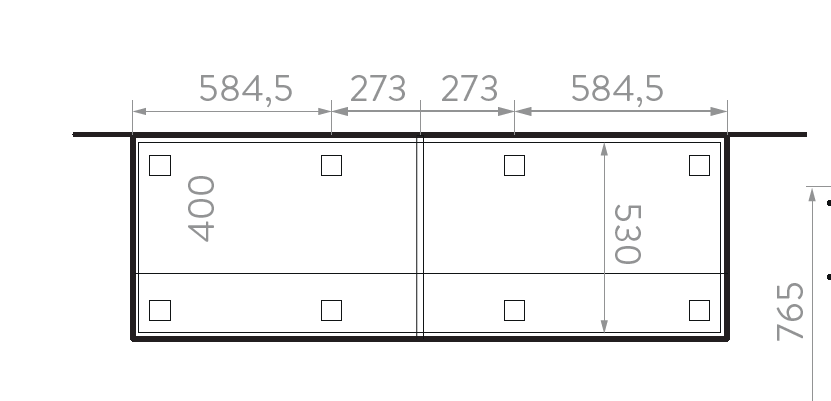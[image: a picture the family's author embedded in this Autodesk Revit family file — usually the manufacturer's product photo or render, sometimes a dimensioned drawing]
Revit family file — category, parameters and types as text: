
# Revit family: O22411711_Cocina Soho Izquierda
name_source: partatom
category: Generic Models
units: mm (PartAtom-declared; Revit-internal decimal feet)

## family parameters
Always vertical = Yes
Can host rebar = No
Cut with Voids When Loaded = No
Host = Wall
OmniClass Number = 23.21.23.23.13
OmniClass Title = Residential Food Cookers
Part Type = Normal
Room Calculation Point = No
Round Connector Dimension = Use Diameter
Shared = No

## types (1)
- Ref. O22411711 Cocina Soho Izquierda
    Alto Mueble Inferior = 926 mm  [stored 3.03806 ft]
    Alto Mueble Superior = 650 mm  [stored 2.13255 ft]
    Ancho Mueble Inferioir = 1760 mm  [stored 5.77428 ft]
    Ancho Mueble Inferior = 1800 mm  [stored 5.90551 ft]
    Carga máxima Campana = 25 kg.
    Carga máxima Mueble Superior = 42 kg.
    Carga máxima mueble inferior = 73 kg.
    Description = Esta cocina de diseño contemporáneo está disponible en color miel, contrastado con detalles en gris plomo. Sus puertas lisas (sin manijas expuestas) aportan limpieza y continuidad al diseño, haciendo que la cocina sea más amigable con el usuario. Esta cocina entrega una solución completa al incluir en su mueble inferior un mesón en CoronaStone® con lavaplatos y cubierta con 4 fogones integrados, además de accesorios como vajillero y cubertero para hacer más cómodo el almacenamiento.En todo el mueble, los cantos o recubrimiento de bordes, cuentan con mayor espesor y rigidez al estándar del mercado, brindando un acabado estético superior y mayor protección a posibles filtraciones de humedad.Disfruta de su máximo almacenamiento y comodidad de uso, y de nuestros muebles altamente resistentes. ¡Una solución integral de fácil instalación!
    Dimensiones generales del mueble inferior (H*W*L) = 920x 1800x 600mm.
    Dimensiones generales mueble rior (H*W*L). = 650 x 345 x 1800 mm.
    Garantia Mesón = 10 años
    Garantía de Herrajes = 1 año
    Garantía de madera = 1 año
    Material Patas = Corona_Acero inoxidable
    Material meson = Corona_Cuarzo_Natural
    Material mueble inferior = Corona_Madera_Blanco
    Material mueble superior = Corona_Madera_Blanco
    Material puertas A = Corona_Madera_Aglomerada_Miel
    Material puertas B = Corona_Madera_Aglomerada_Plomo
    Peso Neto aproximado mueble inferior = 63 kg.
    Peso Neto aproximado mueble superior = 41,29 kg.
    Pofundidad Mueble Inferior = 595 mm  [stored 1.9521 ft]
    Pofundidad Mueble Superioir = 345 mm  [stored 1.13189 ft]
    Resistencia a la humedad = Hinchamiento < o =8%.
    URL = https://corona.co

note: [stored X ft] marks values corroborated as IEEE doubles in the binary element streams (Revit-internal decimal feet)

## geometry (parser evidence)
native form markers: Sweep x12
no freeform markers — native parametric forms only
